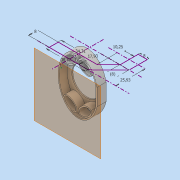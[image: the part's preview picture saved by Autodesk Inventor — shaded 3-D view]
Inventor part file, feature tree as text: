
AUTODESK INVENTOR PART (.ipt)
format: ipt  version: 2019 (Build 230136000, 136)  size: 301,568 bytes
history: native  units: mm
features: other x2, sketch x2, extrude x2, shell x2, chamfer x1
ambient origin geometry x8: Origin, YZ Plane, XZ Plane, XY Plane, X Axis, Y Axis, Z Axis, Center Point
bodies: Body1 (feature_tree), Body2 (feature_tree)
feature tree (9):
  other  "Твердое тело1"
  sketch  "Эскиз1"
  extrude  "Выдавливание1"  Depth=34.31mm
  sketch  "Эскиз7"
  shell  "сам корпус"  Thickness=8.0mm
  extrude  "Выдавливание10"  Depth=34.31mm
  shell  "Оболочка9"  Thickness=8.0mm
  chamfer  "Фаска1"  Distance=17.93mm
  other  "Твердое тело6"
